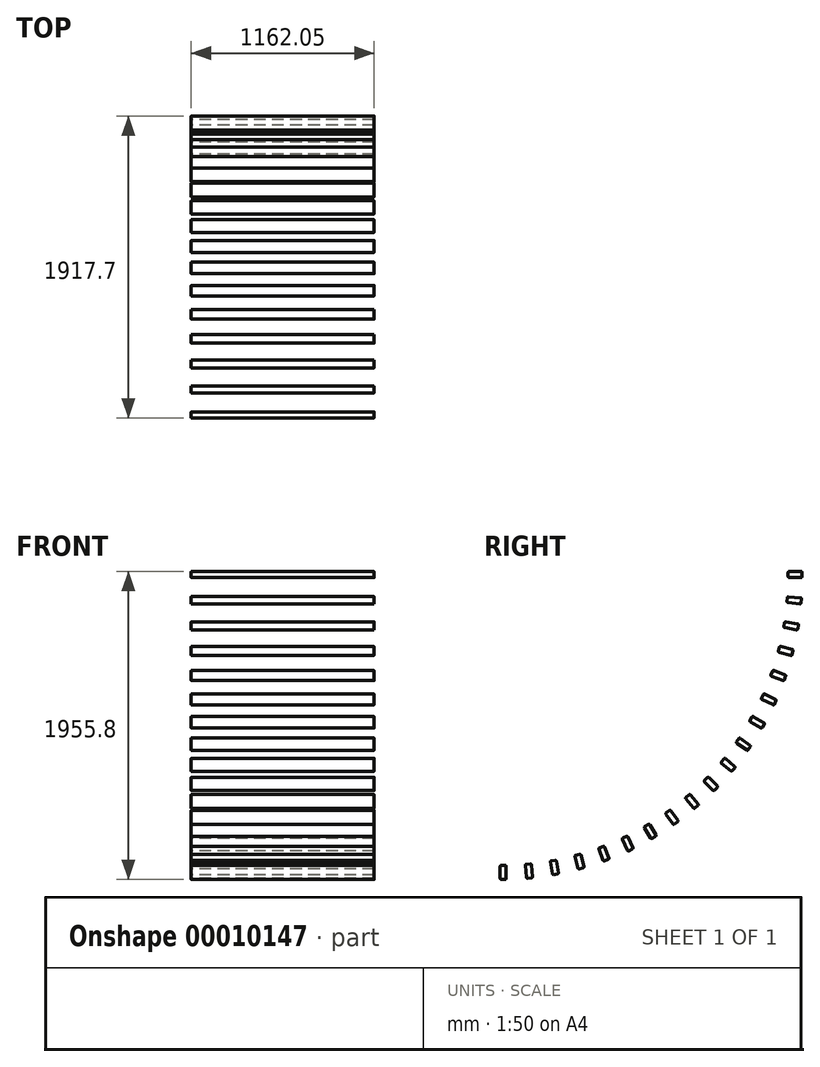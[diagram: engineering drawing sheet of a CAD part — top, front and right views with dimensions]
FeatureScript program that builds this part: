
annotation { "Feature Type Name" : "Feature", "Feature Type Description" : "" }
export const myFeature = defineFeature(function(context is Context, id is Id, definition is map)
    precondition{}
    {
        {
            var Q0;
            Q0=qCreatedBy(makeId("Right.planeOp"),FACE);
            var sketch = newSketch(context, id + "F0", { "sketchPlane" : qUnion([Q0])});
            skLineSegment(sketch, "E0", {"start": v(0, 6.35) * mm, "end": v(0, 82.55) * mm});
            skLineSegment(sketch, "E1", {"start": v(6.35, 88.9) * mm, "end": v(31.75, 88.9) * mm});
            skLineSegment(sketch, "E2", {"start": v(38.1, 82.55) * mm, "end": v(38.1, 6.35) * mm});
            skLineSegment(sketch, "E3", {"start": v(31.75, 0) * mm, "end": v(6.35, 0) * mm});
            skPoint(sketch, "E4.visualSharp", {"position": v(0, 88.9) * mm});
            skArc(sketch, "E4.filletArc", {"start": v(6.35, 88.9) * mm, "mid": v(1.86, 87.04) * mm, "end": v(0, 82.55) * mm});
            skPoint(sketch, "E5.visualSharp", {"position": v(38.1, 88.9) * mm});
            skArc(sketch, "E5.filletArc", {"start": v(38.1, 82.55) * mm, "mid": v(36.24, 87.04) * mm, "end": v(31.75, 88.9) * mm});
            skPoint(sketch, "E6.visualSharp", {"position": v(38.1, 0) * mm});
            skArc(sketch, "E6.filletArc", {"start": v(31.75, 0) * mm, "mid": v(36.24, 1.86) * mm, "end": v(38.1, 6.35) * mm});
            skPoint(sketch, "E7.visualSharp", {"position": v(0, 0) * mm});
            skArc(sketch, "E7.filletArc", {"start": v(0, 6.35) * mm, "mid": v(1.86, 1.86) * mm, "end": v(6.35, 0) * mm});
            skSolve(sketch);
        }
        {
            var Q0;
            Q0 = qSketchRegion(id + "F0", true);
            extrude(context, id + "F1", {"entities" : qUnion([Q0]), "depth" : 1181.1 * mm});
        }
        {
            var Q0;
            Q0 = qSketchRegion(id + "F0", true);
            extrude(context, id + "F2", {"entities" : qUnion([Q0]), "operationType" : NewBodyOperationType.REMOVE, "depth" : 19.05 * mm});
        }
        {
            var Q0;
            Q0=qCreatedBy(makeId("Front.planeOp"),FACE);
            var sketch = newSketch(context, id + "F3", { "sketchPlane" : qUnion([Q0])});
            skLineSegment(sketch, "E8", {"start": v(0, 0) * mm, "end": v(0, 1917.7) * mm});
            skLineSegment(sketch, "E9", {"start": v(0, 1917.7) * mm, "end": v(1583.83, 1917.7) * mm});
            skSolve(sketch);
        }
        {
            var Q0;
            Q0=makeQuery(id+"F1.opExtrude","SWEPT_BODY",BODY,{"disambiguationData":[OSD([sQuery(id+"F0.wireOp",EDGE,"E0"),sQuery(id+"F0.wireOp",EDGE,"E1"),sQuery(id+"F0.wireOp",EDGE,"E2"),sQuery(id+"F0.wireOp",EDGE,"E3"),sQuery(id+"F0.wireOp",EDGE,"E4.filletArc"),sQuery(id+"F0.wireOp",EDGE,"E5.filletArc"),sQuery(id+"F0.wireOp",EDGE,"E6.filletArc"),sQuery(id+"F0.wireOp",EDGE,"E7.filletArc")])]});
            var Q1;
            Q1=sQuery(id+"F3.wireOp",EDGE,"E9");
            circularPattern(context, id + "F4", {"entities" : qUnion([Q0]), "axis" : qUnion([Q1]), "angle" : 5 * degree, "instanceCount" : 19});
        }
    });
